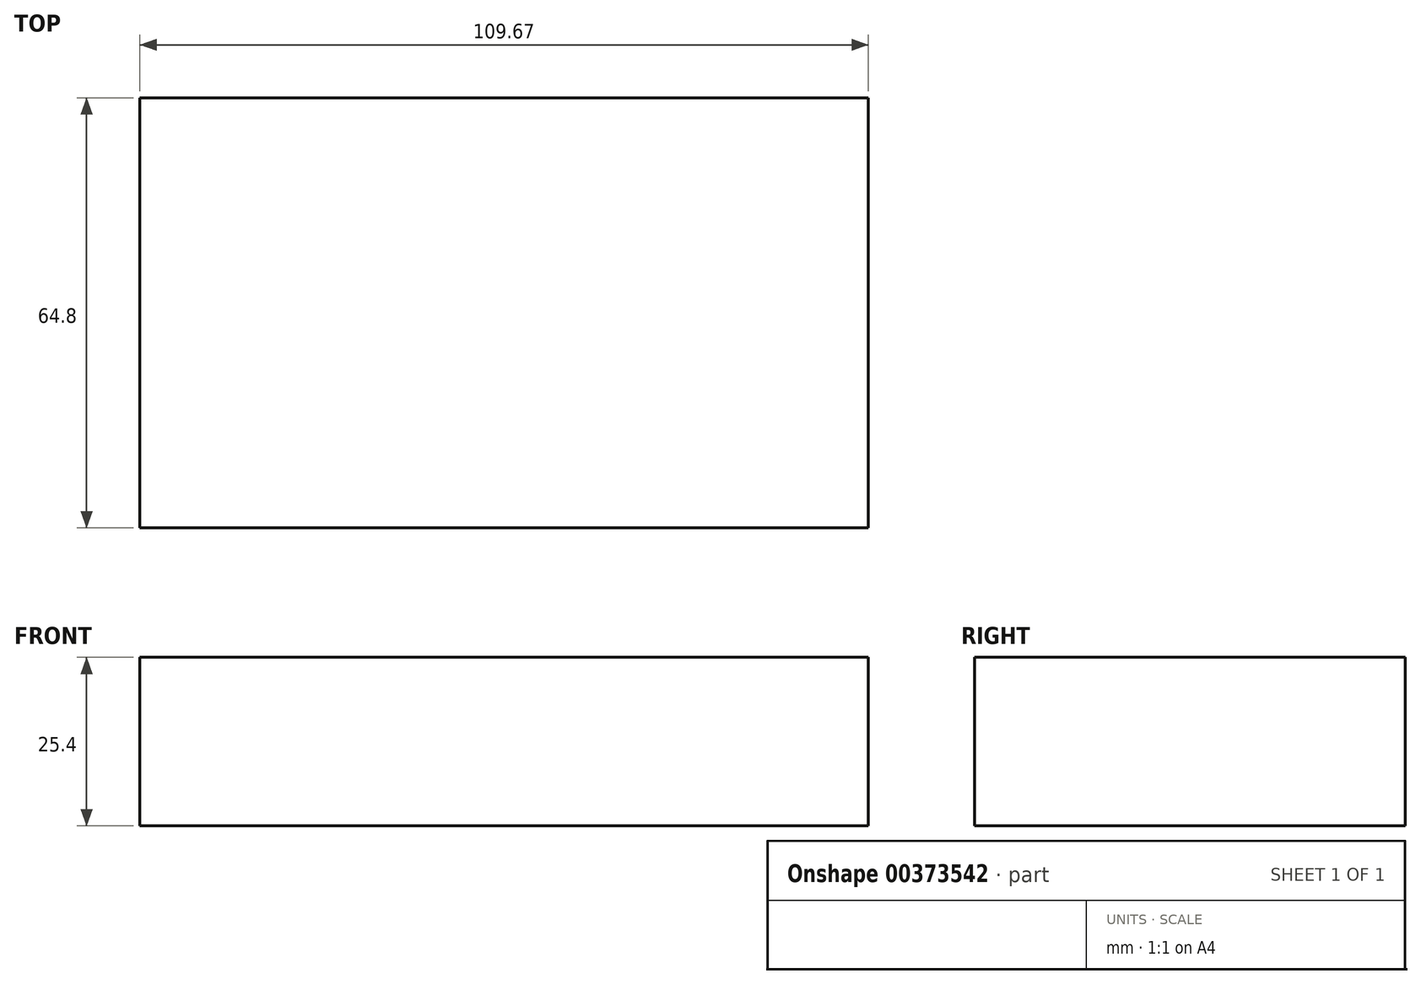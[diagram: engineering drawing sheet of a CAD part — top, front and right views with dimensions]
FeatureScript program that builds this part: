
annotation { "Feature Type Name" : "Feature", "Feature Type Description" : "" }
export const myFeature = defineFeature(function(context is Context, id is Id, definition is map)
    precondition{}
    {
        {
            var Q0;
            Q0=qCreatedBy(makeId("Top.planeOp"),FACE);
            var sketch = newSketch(context, id + "F0", { "sketchPlane" : qUnion([Q0])});
            skLineSegment(sketch, "E0.bottom", {"start": v(-59.73, 35.84) * mm, "end": v(49.94, 35.84) * mm});
            skLineSegment(sketch, "E0.top", {"start": v(-59.73, -28.96) * mm, "end": v(49.94, -28.96) * mm});
            skLineSegment(sketch, "E0.left", {"start": v(-59.73, 35.84) * mm, "end": v(-59.73, -28.96) * mm});
            skLineSegment(sketch, "E0.right", {"start": v(49.94, 35.84) * mm, "end": v(49.94, -28.96) * mm});
            skSolve(sketch);
        }
        {
            var Q0;
            Q0 = qSketchRegion(id + "F0", true);
            extrude(context, id + "F1", {"entities" : qUnion([Q0]), "depth" : 25.4 * mm});
        }
    });
